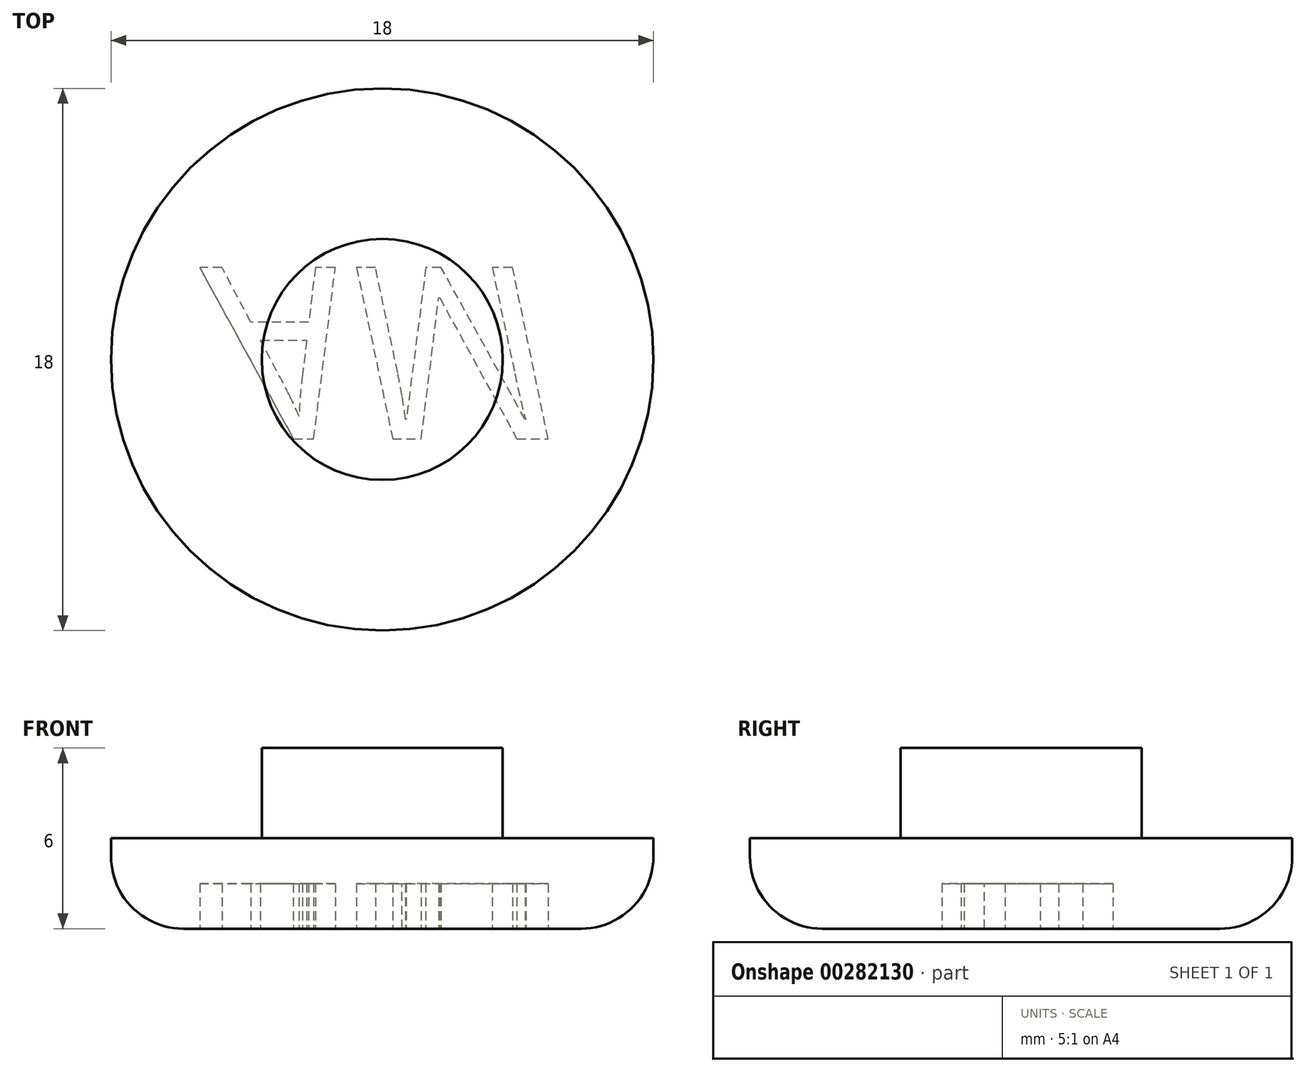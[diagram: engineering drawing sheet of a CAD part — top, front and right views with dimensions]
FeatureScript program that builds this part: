
annotation { "Feature Type Name" : "Feature", "Feature Type Description" : "" }
export const myFeature = defineFeature(function(context is Context, id is Id, definition is map)
    precondition{}
    {
        {
            var Q0;
            Q0=qCreatedBy(makeId("Top.planeOp"),FACE);
            var sketch = newSketch(context, id + "F0", { "sketchPlane" : qUnion([Q0])});
            skCircle(sketch, "E0", {"center": v(0, 0) * mm, "radius": 9 * mm});
            skSolve(sketch);
        }
        {
            var Q0;
            Q0 = qSketchRegion(id + "F0", true);
            extrude(context, id + "F1", {"entities" : qUnion([Q0]), "depth" : 3 * mm});
        }
        {
            var Q0;
            Q0=makeQuery(id+"F1.opExtrude","CAP_FACE",FACE,{"disambiguationData":[OSD([sQuery(id+"F0.wireOp",EDGE,"E0")])],"isStart":false});
            var sketch = newSketch(context, id + "F2", { "sketchPlane" : qUnion([Q0])});
            skCircle(sketch, "E1", {"center": v(0, 0) * mm, "radius": 4 * mm});
            skSolve(sketch);
        }
        {
            var Q0;
            Q0 = qSketchRegion(id + "F2", true);
            extrude(context, id + "F3", {"entities" : qUnion([Q0]), "operationType" : NewBodyOperationType.ADD, "depth" : 3 * mm, "offsetDistance" : 25 * mm});
        }
        {
            var Q0;
            Q0=makeQuery(id+"F1.opExtrude","CAP_EDGE",EDGE,{"disambiguationData":[OSD([sQuery(id+"F0.wireOp",EDGE,"E0")])],"isStart":true});
            fillet(context, id + "F4", {"entities" : qUnion([Q0]), "radius" : 2.4 * mm, "tangentPropagation" : true, "allowEdgeOverflow" : false});
        }
        {
            var Q0;
            Q0=makeQuery(id+"F1.opExtrude","CAP_FACE",FACE,{"disambiguationData":[OSD([sQuery(id+"F0.wireOp",EDGE,"E0")])],"isStart":true});
            var sketch = newSketch(context, id + "F5", { "sketchPlane" : qUnion([Q0])});
            skText(sketch, "E2", { "text": "AM\n", "fontName": "OpenSans-Italic.ttf"});
            const initialGuessF5  = {"E2": [-0.0056, -0.00305, 1, 0, 0.00573]};
            skSetInitialGuess(sketch, initialGuessF5);
            skSolve(sketch);
        }
        {
            var Q0;
            Q0 = qSketchRegion(id + "F5", true);
            extrude(context, id + "F6", {"entities" : qUnion([Q0]), "operationType" : NewBodyOperationType.REMOVE, "oppositeDirection" : true, "depth" : 1.5 * mm, "offsetDistance" : 25 * mm});
        }
    });
